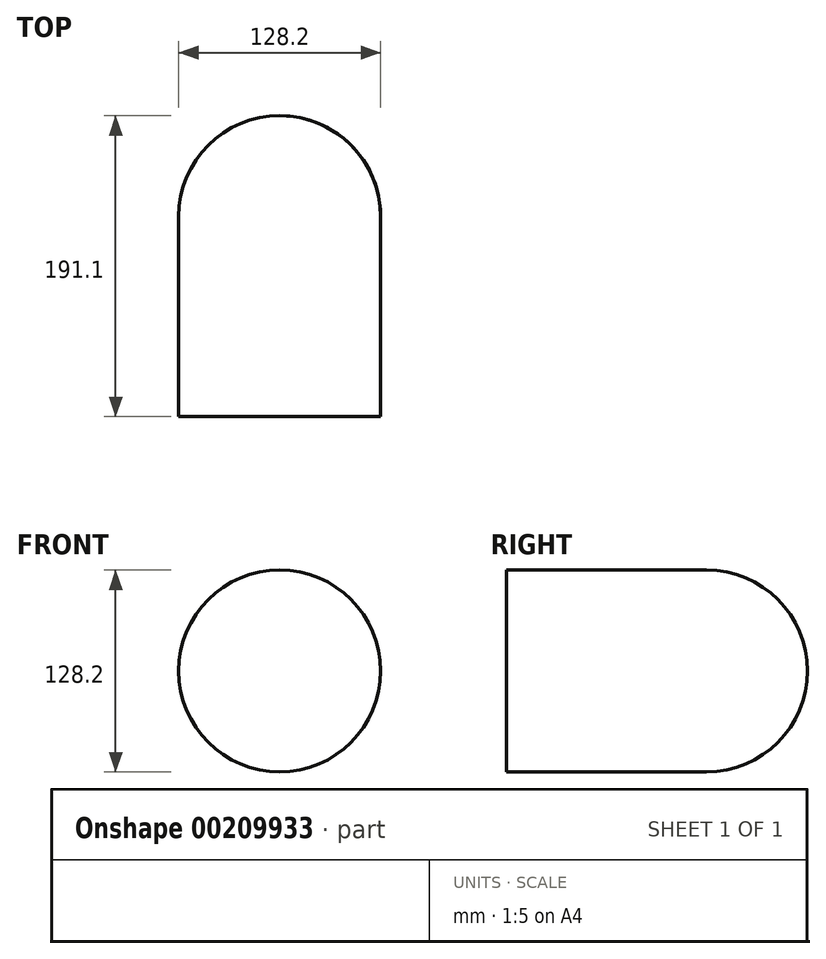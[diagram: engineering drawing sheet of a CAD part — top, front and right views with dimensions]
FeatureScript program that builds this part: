
annotation { "Feature Type Name" : "Feature", "Feature Type Description" : "" }
export const myFeature = defineFeature(function(context is Context, id is Id, definition is map)
    precondition{}
    {
        {
            var Q0;
            Q0=qCreatedBy(makeId("Top.planeOp"),FACE);
            var sketch = newSketch(context, id + "F0", { "sketchPlane" : qUnion([Q0])});
            skLineSegment(sketch, "E0", {"start": v(0, 64.1) * mm, "end": v(0, 0) * mm});
            skLineSegment(sketch, "E1", {"start": v(0, 0) * mm, "end": v(64.1, 0) * mm});
            skLineSegment(sketch, "E2", {"start": v(0, -64.1) * mm, "end": v(0, -64.1) * mm});
            skArc(sketch, "E3", {"start": v(64.1, 0) * mm, "mid": v(45.33, 45.33) * mm, "end": v(0, 64.1) * mm});
            skSolve(sketch);
        }
        {
            var Q0;
            Q0=makeQuery(id+"F0.imprint","IMPRINT",FACE,{"disambiguationData":[TD([[makeQuery(id+"F0.imprint","IMPRINT",EDGE,{"derivedFrom":sQuery(id+"F0.wireOp",EDGE,"E0")}),1.0]])]});
            var Q1;
            Q1=sQuery(id+"F0.wireOp",EDGE,"E0");
            revolve(context, id + "F1", {"entities" : qUnion([Q0]), "axis" : qUnion([Q1]), "revolveType" : RevolveType.FULL});
        }
        {
            var Q0;
            Q0=makeQuery(id+"F1.opRevolve","SWEPT_FACE",FACE,{"disambiguationData":[OSD([sQuery(id+"F0.wireOp",EDGE,"E1")])]});
            extrude(context, id + "F2", {"entities" : qUnion([Q0]), "operationType" : NewBodyOperationType.ADD, "depth" : 127 * mm});
        }
    });
